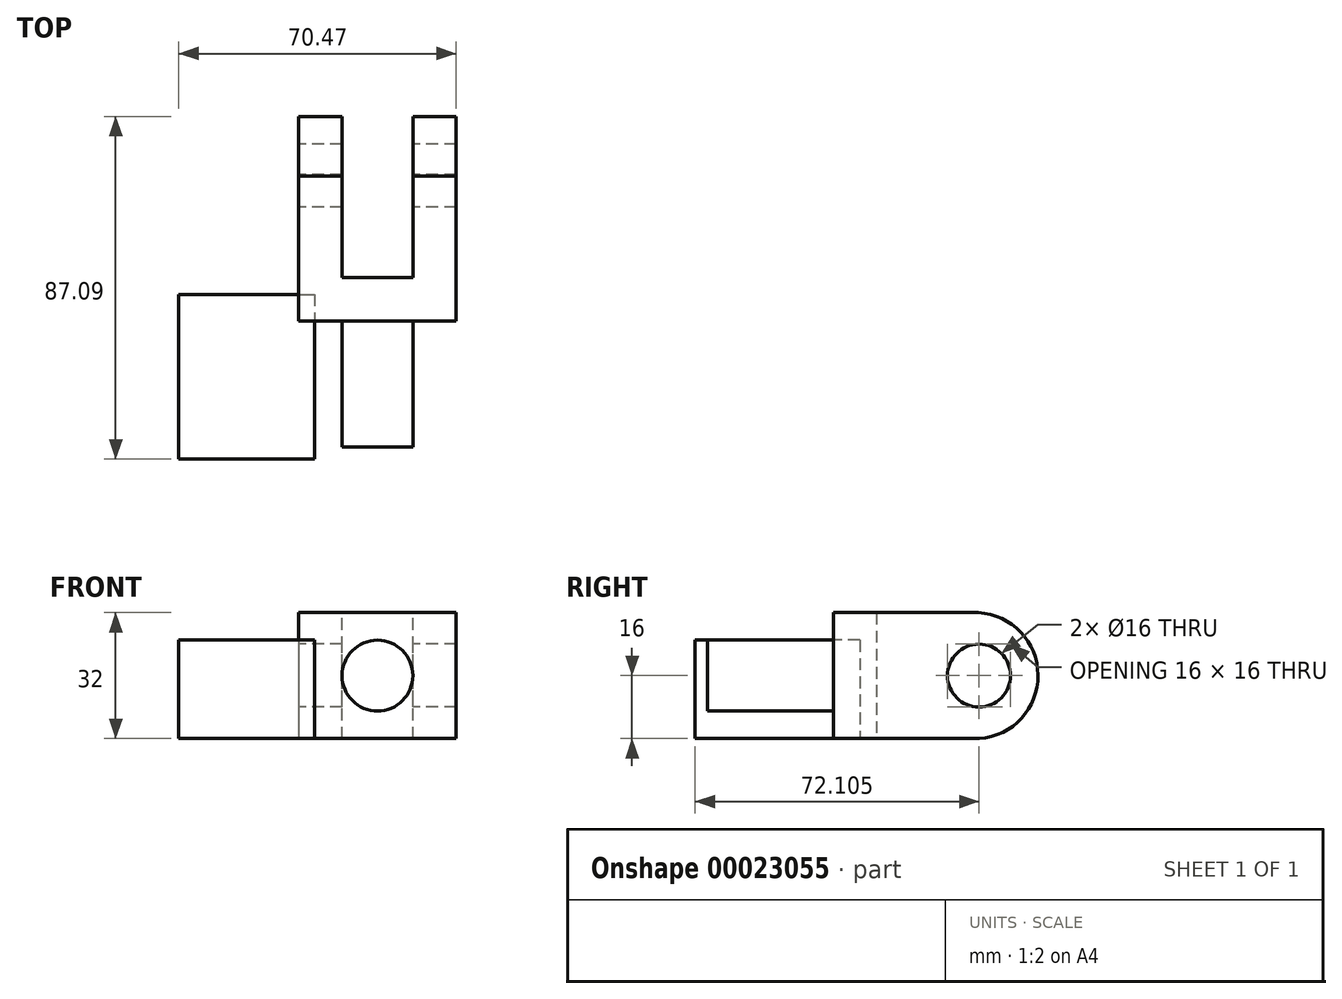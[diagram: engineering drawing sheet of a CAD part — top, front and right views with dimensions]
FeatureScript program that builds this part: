
annotation { "Feature Type Name" : "Feature", "Feature Type Description" : "" }
export const myFeature = defineFeature(function(context is Context, id is Id, definition is map)
    precondition{}
    {
        {
            var Q0;
            Q0=qCreatedBy(makeId("Top.planeOp"),FACE);
            var sketch = newSketch(context, id + "F0", { "sketchPlane" : qUnion([Q0])});
            skLineSegment(sketch, "E0", {"start": v(-30.3, 35) * mm, "end": v(-30.3, -17) * mm});
            skLineSegment(sketch, "E1", {"start": v(-30.3, -17) * mm, "end": v(9.7, -17) * mm});
            skLineSegment(sketch, "E2", {"start": v(9.7, -17) * mm, "end": v(9.7, 35) * mm});
            skLineSegment(sketch, "E3", {"start": v(-30.3, 35) * mm, "end": v(-19.3, 35) * mm});
            skLineSegment(sketch, "E4", {"start": v(9.7, 35) * mm, "end": v(-1.3, 35) * mm});
            skLineSegment(sketch, "E5", {"start": v(-19.3, 35) * mm, "end": v(-19.3, -6) * mm});
            skLineSegment(sketch, "E6", {"start": v(-1.3, 35) * mm, "end": v(-1.3, -6) * mm});
            skLineSegment(sketch, "E7", {"start": v(-19.3, -6) * mm, "end": v(-1.3, -6) * mm});
            skSolve(sketch);
        }
        {
            var Q0;
            Q0 = qSketchRegion(id + "F0", true);
            extrude(context, id + "F1", {"entities" : qUnion([Q0]), "depth" : 32 * mm});
        }
        {
            var Q0;
            Q0=makeQuery(id+"F1.opExtrude","SWEPT_FACE",FACE,{"disambiguationData":[OSD([sQuery(id+"F0.wireOp",EDGE,"E0")])]});
            var sketch = newSketch(context, id + "F2", { "sketchPlane" : qUnion([Q0])});
            skCircle(sketch, "E8", {"center": v(-18.96, 16) * mm, "radius": 16.03 * mm});
            skPoint(sketch, "E8.first.point", {"position": v(-19.87, 32) * mm});
            skPoint(sketch, "E8.second.point", {"position": v(-35, 16) * mm});
            skPoint(sketch, "E8.third.point", {"position": v(-17.78, 0) * mm});
            skSolve(sketch);
        }
        {
            var Q0;
            {var subQ0=sQuery(id+"F0.wireOp",EDGE,"E0");var subQ1=makeQuery(id+"F1.opExtrude","CAP_EDGE",EDGE,{"disambiguationData":[OSD([subQ0])],"isStart":false});var subQ2=sQuery(id+"F2.wireOp",EDGE,"E8");var subQ3=makeQuery(id+"F2.imprint","INTERSECT",VERTEX,{"disambiguationData":[OD(0.0)],"derivedFrom":[subQ1,subQ2]});Q0=makeQuery(id+"F2.imprint","IMPRINT",FACE,{"disambiguationData":[TD([[makeQuery(id+"F2.imprint","IMPRINT",EDGE,{"disambiguationData":[TD([[subQ3,-1.0]])],"derivedFrom":subQ2}),-1.0]])]});}
            var Q1;
            {var subQ0=sQuery(id+"F0.wireOp",EDGE,"E0");var subQ1=makeQuery(id+"F1.opExtrude","CAP_EDGE",EDGE,{"disambiguationData":[OSD([subQ0])],"isStart":true});var subQ2=sQuery(id+"F2.wireOp",EDGE,"E8");var subQ3=makeQuery(id+"F2.imprint","INTERSECT",VERTEX,{"disambiguationData":[OD(0.0)],"derivedFrom":[subQ1,subQ2]});Q1=makeQuery(id+"F2.imprint","IMPRINT",FACE,{"disambiguationData":[TD([[makeQuery(id+"F2.imprint","IMPRINT",EDGE,{"disambiguationData":[TD([[subQ3,1.0]])],"derivedFrom":subQ2}),-1.0]])]});}
            extrude(context, id + "F3", {"entities" : qUnion([Q0, Q1]), "operationType" : NewBodyOperationType.REMOVE, "endBound" : BoundingType.THROUGH_ALL, "oppositeDirection" : true, "depth" : 25 * mm});
        }
        {
            var Q0;
            Q0=makeQuery(id+"F1.opExtrude","SWEPT_FACE",FACE,{"disambiguationData":[OSD([sQuery(id+"F0.wireOp",EDGE,"E0")])]});
            var sketch = newSketch(context, id + "F4", { "sketchPlane" : qUnion([Q0])});
            skCircle(sketch, "E9", {"center": v(-20, 16) * mm, "radius": 8 * mm});
            skSolve(sketch);
        }
        {
            var Q0;
            Q0=makeQuery(id+"F4.imprint","IMPRINT",FACE,{"disambiguationData":[TD([[makeQuery(id+"F4.imprint","IMPRINT",EDGE,{"derivedFrom":sQuery(id+"F4.wireOp",EDGE,"E9")}),1.0]])]});
            extrude(context, id + "F5", {"entities" : qUnion([Q0]), "operationType" : NewBodyOperationType.REMOVE, "endBound" : BoundingType.THROUGH_ALL, "oppositeDirection" : true, "depth" : 25 * mm});
        }
        {
            var Q0;
            Q0=makeQuery(id+"F1.opExtrude","SWEPT_FACE",FACE,{"disambiguationData":[OSD([sQuery(id+"F0.wireOp",EDGE,"E1")])]});
            var sketch = newSketch(context, id + "F6", { "sketchPlane" : qUnion([Q0])});
            skLineSegment(sketch, "E10", {"start": v(-10.3, 32) * mm, "end": v(-10.3, 0) * mm, "construction": true});
            skLineSegment(sketch, "E11", {"start": v(-10.3, 0) * mm, "end": v(-30.3, 16) * mm, "construction": true});
            skLineSegment(sketch, "E12", {"start": v(-30.3, 16) * mm, "end": v(9.7, 16) * mm, "construction": true});
            skLineSegment(sketch, "E13", {"start": v(9.7, 16) * mm, "end": v(-10.3, 0) * mm, "construction": true});
            skLineSegment(sketch, "E14", {"start": v(-10.3, 32) * mm, "end": v(-30.3, 16) * mm, "construction": true});
            skLineSegment(sketch, "E15", {"start": v(-10.3, 32) * mm, "end": v(9.7, 16) * mm, "construction": true});
            skCircle(sketch, "E16", {"center": v(-10.3, 16) * mm, "radius": 9 * mm});
            skSolve(sketch);
        }
        {
            var Q0;
            Q0=makeQuery(id+"F6.imprint","IMPRINT",FACE,{"disambiguationData":[TD([[makeQuery(id+"F6.imprint","IMPRINT",EDGE,{"derivedFrom":sQuery(id+"F6.wireOp",EDGE,"E16")}),1.0]])]});
            extrude(context, id + "F7", {"entities" : qUnion([Q0]), "operationType" : NewBodyOperationType.ADD, "depth" : 32 * mm});
        }
        {
            var Q0;
            Q0=qCreatedBy(makeId("Top.planeOp"),FACE);
            var sketch = newSketch(context, id + "F8", { "sketchPlane" : qUnion([Q0])});
            skLineSegment(sketch, "E17.bottom", {"start": v(-60.78, -10.26) * mm, "end": v(-26.33, -10.26) * mm});
            skLineSegment(sketch, "E17.top", {"start": v(-60.78, -52.1) * mm, "end": v(-26.33, -52.1) * mm});
            skLineSegment(sketch, "E17.left", {"start": v(-60.78, -10.26) * mm, "end": v(-60.78, -52.1) * mm});
            skLineSegment(sketch, "E17.right", {"start": v(-26.33, -10.26) * mm, "end": v(-26.33, -52.1) * mm});
            skSolve(sketch);
        }
        {
            var Q0;
            Q0 = qSketchRegion(id + "F8", true);
            extrude(context, id + "F9", {"entities" : qUnion([Q0]), "depth" : 25 * mm});
        }
    });
